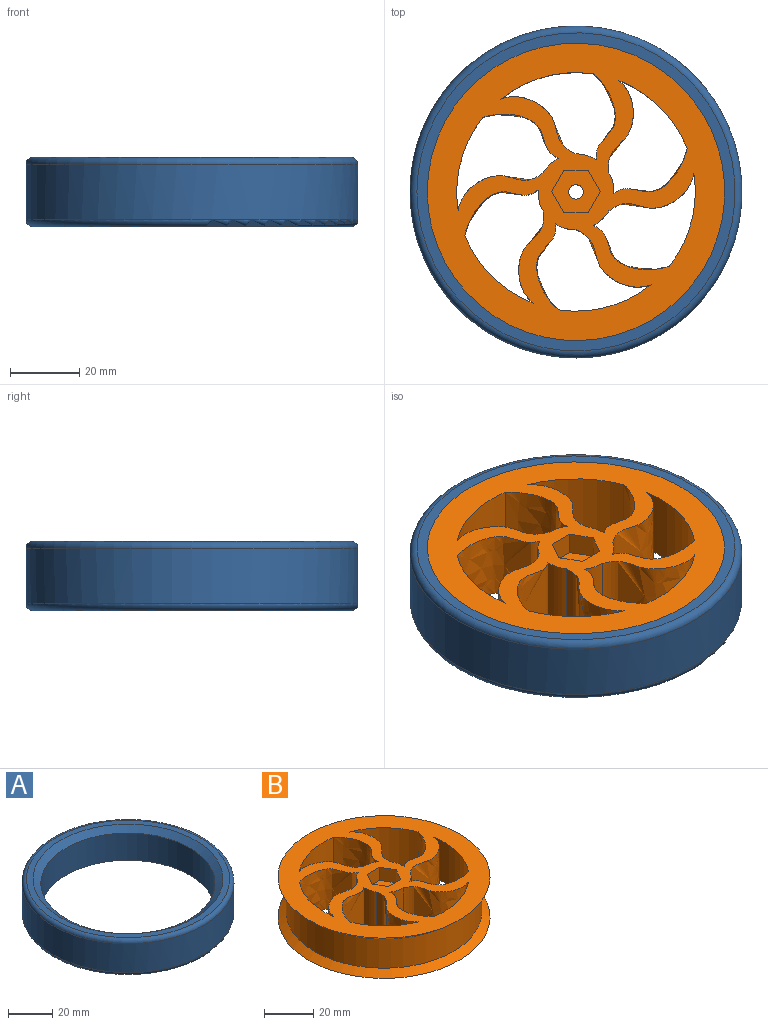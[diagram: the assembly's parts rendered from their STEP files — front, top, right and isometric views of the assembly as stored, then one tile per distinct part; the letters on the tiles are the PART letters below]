
ASSEMBLY  parts=2 mates=1
PART A: 8 faces, bbox 103.9x103.9x20 mm
  f0: cone r=39.47mm half-angle=55.2deg, axis (0,0,1), area 1114.1mm2, adj f1,f5
  f1: cylinder r=39.47mm len=78.94mm, axis (0,0,-1), area 3742mm2, adj f0,f2
  f2: cone r=43mm half-angle=55.2deg, axis (0,0,-1), area 1114.1mm2, adj f1,f3
  f3: plane 92x92mm, normal (0,0,-1), area 838.8mm2, adj f2,f6
  f4: cylinder r=48mm len=96mm, axis (0,0,-1), area 4825.5mm2, adj f6,f7
  f5: plane 92x92mm, normal (0,0,1), area 838.8mm2, adj f0,f7
  f6: torus R=46mm, axis (0,0,1), area 933.1mm2, adj f3,f4
  f7: torus R=46mm, axis (0,0,-1), area 933.1mm2, adj f4,f5
PART B: 38 faces, bbox 86x86x20 mm
  f0: plane 86x86mm, normal (0,0,1), area 3123.9mm2, adj f4,f5,f6,f7,f8,f9,f10,f14
  f1: plane 86x86mm, normal (0,0,-1), area 3208.6mm2, adj f2,f13,f14,f15,f16,f17,f18,f19
  f2: cone r=39.69mm half-angle=50.2deg, axis (0,0,-1), area 1117.1mm2, adj f1,f3
  f3: cylinder r=39.69mm len=79.39mm, axis (0,0,-1), area 3616.4mm2, adj f2,f4
  f4: cone r=43mm half-angle=50.2deg, axis (0,0,1), area 1117.1mm2, adj f0,f3
  f5: plane 7.04x6.5mm, normal (0,-1,0), area 45.8mm2, adj f0,f6,f10,f11
  f6: plane 6.5x6.1mm, normal (0.87,-0.5,0), area 45.8mm2, adj f0,f5,f7,f11
  f7: plane 6.5x6.1mm, normal (0.87,0.5,0), area 45.8mm2, adj f0,f6,f8,f11
  f8: plane 7.04x6.5mm, normal (0,1,0), area 45.8mm2, adj f0,f7,f9,f11
  f9: plane 6.5x6.1mm, normal (-0.87,0.5,0), area 45.8mm2, adj f0,f8,f10,f11
  f10: plane 6.5x6.1mm, normal (-0.87,-0.5,0), area 45.8mm2, adj f0,f5,f9,f11
  f11: plane 14.09x12.2mm, normal (0,0,1), area 115mm2, adj f5,f6,f7,f8,f9,f10,f12
  f12: cylinder r=2.1mm len=11.85mm, axis (0,0,-1), area 156.4mm2, adj f11,f13
  f13: cone r=2.1mm half-angle=45deg, axis (0,0,-1), area 42.9mm2, adj f1,f12
  f14: extruded ~21.7x20mm, area 603.4mm2, adj f0,f1,f15,f17
  f15: cylinder r=34.5mm len=26.87mm, axis (0,0,-1), area 573.3mm2, adj f0,f1,f14,f16
  f16: extruded ~24.85x20mm, area 567.5mm2, adj f0,f1,f15,f17
  f17: cylinder r=11mm len=20mm, axis (0,0,-1), area 125.5mm2, adj f0,f1,f14,f16
  f18: extruded ~26.71x20mm, area 603.4mm2, adj f0,f1,f19,f21
  f19: cylinder r=34.5mm len=20mm, axis (0,0,-1), area 573.3mm2, adj f0,f1,f18,f20
  f20: extruded ~21.14x20mm, area 567.5mm2, adj f0,f1,f19,f21
  f21: cylinder r=11mm len=20mm, axis (0,0,-1), area 125.5mm2, adj f0,f1,f18,f20
  f22: extruded ~26.71x20mm, area 603.4mm2, adj f0,f1,f23,f25
  f23: cylinder r=34.5mm len=20mm, axis (0,0,-1), area 573.3mm2, adj f0,f1,f22,f24
  f24: extruded ~21.14x20mm, area 567.5mm2, adj f0,f1,f23,f25
  f25: cylinder r=11mm len=20mm, axis (0,0,-1), area 125.5mm2, adj f0,f1,f22,f24
  f26: extruded ~24.55x20mm, area 603.4mm2, adj f0,f1,f27,f29
  f27: cylinder r=34.5mm len=26.92mm, axis (0,0,-1), area 573.3mm2, adj f0,f1,f26,f28
  f28: extruded ~21.91x20mm, area 567.5mm2, adj f0,f1,f27,f29
  f29: cylinder r=11mm len=20mm, axis (0,0,-1), area 125.5mm2, adj f0,f1,f26,f28
  f30: extruded ~24.55x20mm, area 603.4mm2, adj f0,f1,f31,f33
  f31: cylinder r=34.5mm len=26.92mm, axis (0,0,-1), area 573.3mm2, adj f0,f1,f30,f32
  f32: extruded ~21.91x20mm, area 567.5mm2, adj f0,f1,f31,f33
  f33: cylinder r=11mm len=20mm, axis (0,0,-1), area 125.5mm2, adj f0,f1,f30,f32
  f34: extruded ~21.7x20mm, area 603.4mm2, adj f0,f1,f35,f37
  f35: cylinder r=34.5mm len=26.87mm, axis (0,0,-1), area 573.3mm2, adj f0,f1,f34,f36
  f36: extruded ~24.85x20mm, area 567.5mm2, adj f0,f1,f35,f37
  f37: cylinder r=11mm len=20mm, axis (0,0,-1), area 125.5mm2, adj f0,f1,f34,f36
PLACE A t=(-5.25,9.62,57.32)mm
PLACE B t=(-5.25,9.62,57.32)mm
MATE fastened B.f2 <-> A.f0  axis (0,0,-1) through (-5.25,9.62,57.32)mm
